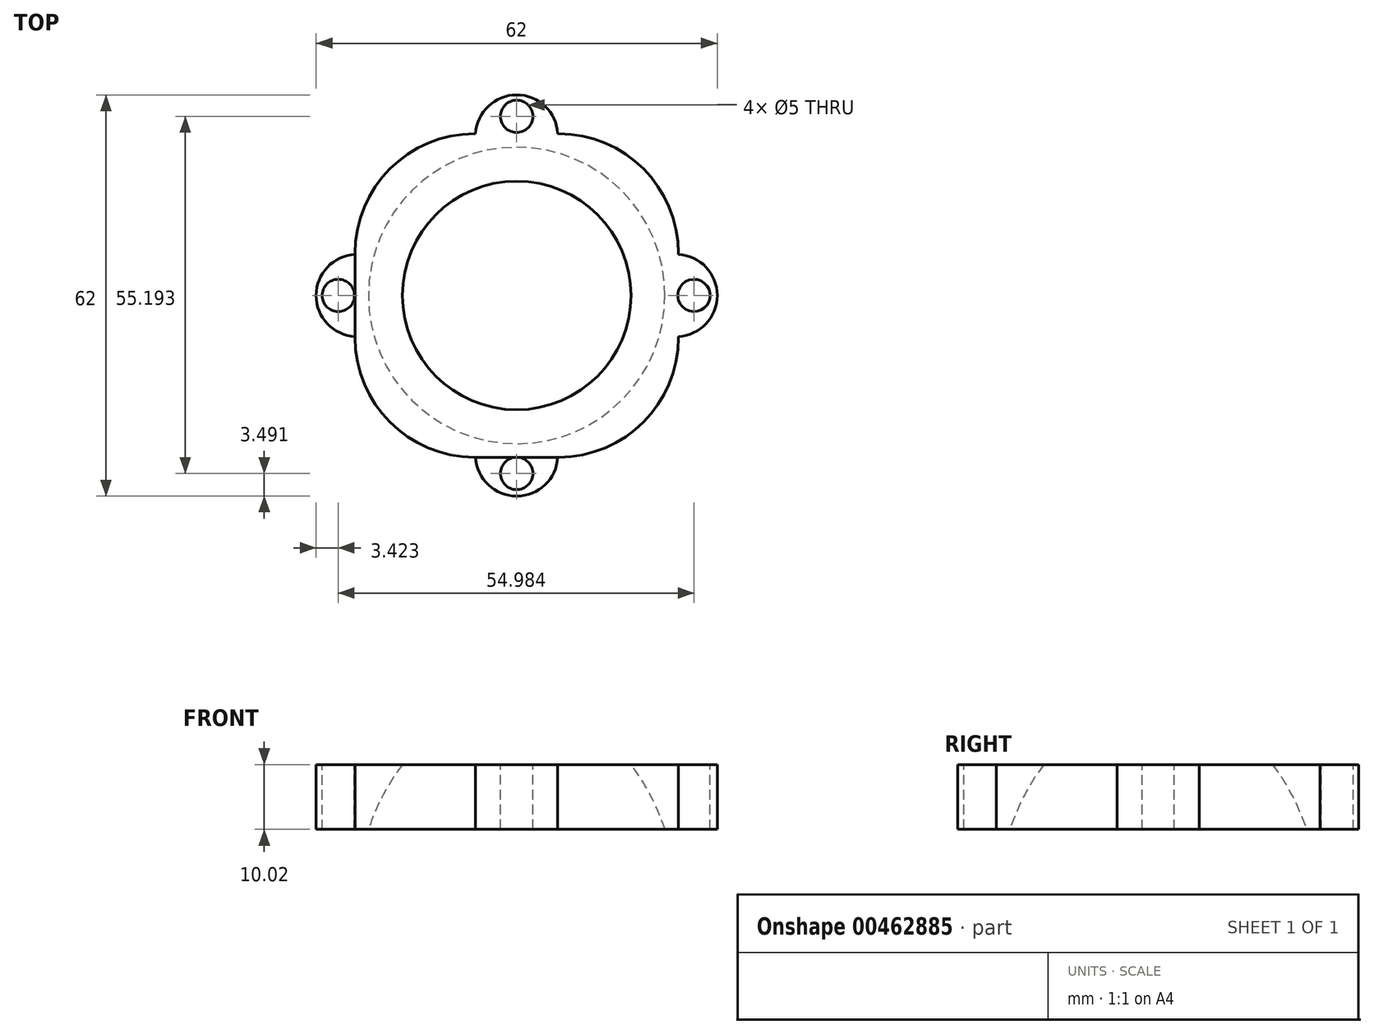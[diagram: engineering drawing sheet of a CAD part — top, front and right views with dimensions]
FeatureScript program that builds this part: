
annotation { "Feature Type Name" : "Feature", "Feature Type Description" : "" }
export const myFeature = defineFeature(function(context is Context, id is Id, definition is map)
    precondition{}
    {
        {
            var Q0;
            Q0=qCreatedBy(makeId("Front.planeOp"),FACE);
            var sketch = newSketch(context, id + "F0", { "sketchPlane" : qUnion([Q0])});
            skEllipticalArc(sketch, "E0", {});
            skLineSegment(sketch, "E1", {"start": v(0, 0) * mm, "end": v(0, 32.5) * mm});
            skLineSegment(sketch, "E2", {"start": v(0, 32.5) * mm, "end": v(0, -32.5) * mm});
            skLineSegment(sketch, "E3", {"start": v(0, 0) * mm, "end": v(25, 0) * mm});
            const initialGuessF0  = {"E0": [0, 0, 0, -1, 0.0325, 0.025, 0, 3.141592653589793]};
            skSetInitialGuess(sketch, initialGuessF0);
            skSolve(sketch);
        }
        {
            var Q0;
            {var subQ0=sQuery(id+"F0.wireOp",EDGE,"E0");Q0=makeQuery(id+"F0.imprint","IMPRINT",FACE,{"disambiguationData":[TD([[makeQuery(id+"F0.imprint","IMPRINT",EDGE,{"derivedFrom":subQ0}),1.0]])]});}
            var Q1;
            Q1=sQuery(id+"F0.wireOp",EDGE,"E2");
            revolve(context, id + "F1", {"entities" : qUnion([Q0]), "axis" : qUnion([Q1]), "revolveType" : RevolveType.FULL});
        }
        {
            var Q0;
            Q0=qCreatedBy(makeId("Top.planeOp"),FACE);
            cPlane(context, id + "F2", {"entities" : qUnion([Q0]), "cplaneType" : CPlaneType.OFFSET, "offset" : 13 * mm, "width" : 152.4 * mm, "height" : 152.4 * mm});
        }
        {
            var Q0;
            Q0=qCreatedBy(id+"F2.planeOp",FACE);
            var sketch = newSketch(context, id + "F3", { "sketchPlane" : qUnion([Q0])});
            skLineSegment(sketch, "E4.bottom", {"start": v(25, -25) * mm, "end": v(-25, -25) * mm});
            skLineSegment(sketch, "E4.top", {"start": v(25, 25) * mm, "end": v(-25, 25) * mm});
            skLineSegment(sketch, "E4.left", {"start": v(25, -25) * mm, "end": v(25, 25) * mm});
            skLineSegment(sketch, "E4.right", {"start": v(-25, -25) * mm, "end": v(-25, 25) * mm});
            skPoint(sketch, "E4.middle", {"position": v(0, 0) * mm});
            skSolve(sketch);
        }
        {
            var Q0;
            Q0=qSketchRegion(id+"F3",true);
            extrude(context, id + "F4", {"entities" : qUnion([Q0]), "depth" : 10 * mm});
        }
        {
            var Q0;
            Q0=makeQuery(id+"F1.opRevolve","SWEPT_BODY",BODY,{"disambiguationData":[OSD([sQuery(id+"F0.wireOp",EDGE,"E0"),sQuery(id+"F0.wireOp",EDGE,"E2")])]});
            var Q1;
            Q1=makeQuery(id+"F4.opExtrude","SWEPT_BODY",BODY,{"disambiguationData":[OSD([sQuery(id+"F3.wireOp",EDGE,"E4.bottom"),sQuery(id+"F3.wireOp",EDGE,"E4.top"),sQuery(id+"F3.wireOp",EDGE,"E4.left"),sQuery(id+"F3.wireOp",EDGE,"E4.right")])]});
            booleanBodies(context, id + "F5", {"operationType" : BooleanOperationType.SUBTRACTION, "tools" : qUnion([Q0]), "targets" : qUnion([Q1])});
        }
        {
            var Q0;
            Q0=qCreatedBy(makeId("Front.planeOp"),FACE);
            var Q1;
            Q1=qBodyType(qCreatedBy(id+"F7",EDGE),BodyType.WIRE);
            cPlane(context, id + "F6", {"entities" : qUnion([Q0, Q1]), "cplaneType" : CPlaneType.OFFSET, "offset" : 25 * mm, "width" : 152.4 * mm, "height" : 152.4 * mm});
        }
        {
            var Q0;
            Q0=qCreatedBy(id+"F6.planeOp",FACE);
            var sketch = newSketch(context, id + "F7", { "sketchPlane" : qUnion([Q0])});
            skLineSegment(sketch, "E5.bottom", {"start": v(6.35, 13.01) * mm, "end": v(-6.35, 13.01) * mm});
            skLineSegment(sketch, "E5.top", {"start": v(6.35, 23.01) * mm, "end": v(-6.35, 23.01) * mm});
            skLineSegment(sketch, "E5.left", {"start": v(6.35, 13.01) * mm, "end": v(6.35, 23.01) * mm});
            skLineSegment(sketch, "E5.right", {"start": v(-6.35, 13.01) * mm, "end": v(-6.35, 23.01) * mm});
            skPoint(sketch, "E5.middle", {"position": v(0, 18.01) * mm});
            skSolve(sketch);
        }
        {
            var Q0;
            Q0=makeQuery(id+"F7.imprint","IMPRINT",FACE,{"disambiguationData":[TD([[makeQuery(id+"F7.imprint","IMPRINT",EDGE,{"derivedFrom":sQuery(id+"F7.wireOp",EDGE,"E5.bottom")}),-1.0]])]});
            extrude(context, id + "F8", {"entities" : qUnion([Q0]), "operationType" : NewBodyOperationType.ADD, "depth" : 6 * mm});
        }
        {
            var Q0;
            Q0=qCreatedBy(makeId("Right.planeOp"),FACE);
            cPlane(context, id + "F9", {"entities" : qUnion([Q0]), "cplaneType" : CPlaneType.OFFSET, "offset" : 25 * mm, "width" : 152.4 * mm, "height" : 152.4 * mm});
        }
        {
            var Q0;
            Q0=qCreatedBy(id+"F9.planeOp",FACE);
            var sketch = newSketch(context, id + "F10", { "sketchPlane" : qUnion([Q0])});
            skLineSegment(sketch, "E6.bottom", {"start": v(6.35, 13) * mm, "end": v(-6.35, 13) * mm});
            skLineSegment(sketch, "E6.top", {"start": v(6.35, 23) * mm, "end": v(-6.35, 23) * mm});
            skLineSegment(sketch, "E6.left", {"start": v(6.35, 13) * mm, "end": v(6.35, 23) * mm});
            skLineSegment(sketch, "E6.right", {"start": v(-6.35, 13) * mm, "end": v(-6.35, 23) * mm});
            skPoint(sketch, "E6.middle", {"position": v(0, 18) * mm});
            skSolve(sketch);
        }
        {
            var Q0;
            Q0=makeQuery(id+"F10.imprint","IMPRINT",FACE,{"disambiguationData":[TD([[makeQuery(id+"F10.imprint","IMPRINT",EDGE,{"derivedFrom":sQuery(id+"F10.wireOp",EDGE,"E6.bottom")}),-1.0]])]});
            extrude(context, id + "F11", {"entities" : qUnion([Q0]), "operationType" : NewBodyOperationType.ADD, "depth" : 6 * mm});
        }
        {
            var Q0;
            Q0=qCreatedBy(makeId("Front.planeOp"),FACE);
            cPlane(context, id + "F12", {"entities" : qUnion([Q0]), "cplaneType" : CPlaneType.OFFSET, "offset" : 25 * mm, "oppositeDirection" : true, "width" : 152.4 * mm, "height" : 152.4 * mm});
        }
        {
            var Q0;
            Q0=qCreatedBy(id+"F12.planeOp",FACE);
            var sketch = newSketch(context, id + "F13", { "sketchPlane" : qUnion([Q0])});
            skLineSegment(sketch, "E7.bottom", {"start": v(6.35, 13) * mm, "end": v(-6.35, 13) * mm});
            skLineSegment(sketch, "E7.top", {"start": v(6.35, 23) * mm, "end": v(-6.35, 23) * mm});
            skLineSegment(sketch, "E7.left", {"start": v(6.35, 13) * mm, "end": v(6.35, 23) * mm});
            skLineSegment(sketch, "E7.right", {"start": v(-6.35, 13) * mm, "end": v(-6.35, 23) * mm});
            skPoint(sketch, "E7.middle", {"position": v(0, 18) * mm});
            skSolve(sketch);
        }
        {
            var Q0;
            Q0=makeQuery(id+"F13.imprint","IMPRINT",FACE,{"disambiguationData":[TD([[makeQuery(id+"F13.imprint","IMPRINT",EDGE,{"derivedFrom":sQuery(id+"F13.wireOp",EDGE,"E7.bottom")}),-1.0]])]});
            extrude(context, id + "F14", {"entities" : qUnion([Q0]), "operationType" : NewBodyOperationType.ADD, "oppositeDirection" : true, "depth" : 6 * mm});
        }
        {
            var Q0;
            Q0=qCreatedBy(makeId("Right.planeOp"),FACE);
            cPlane(context, id + "F15", {"entities" : qUnion([Q0]), "cplaneType" : CPlaneType.OFFSET, "offset" : 25 * mm, "oppositeDirection" : true, "width" : 152.4 * mm, "height" : 152.4 * mm});
        }
        {
            var Q0;
            Q0=qCreatedBy(id+"F15.planeOp",FACE);
            var sketch = newSketch(context, id + "F16", { "sketchPlane" : qUnion([Q0])});
            skLineSegment(sketch, "E8.bottom", {"start": v(-6.35, 12.99) * mm, "end": v(6.35, 12.99) * mm});
            skLineSegment(sketch, "E8.top", {"start": v(-6.35, 22.99) * mm, "end": v(6.35, 22.99) * mm});
            skLineSegment(sketch, "E8.left", {"start": v(-6.35, 12.99) * mm, "end": v(-6.35, 22.99) * mm});
            skLineSegment(sketch, "E8.right", {"start": v(6.35, 12.99) * mm, "end": v(6.35, 22.99) * mm});
            skPoint(sketch, "E8.middle", {"position": v(0, 17.99) * mm});
            skSolve(sketch);
        }
        {
            var Q0;
            Q0=makeQuery(id+"F16.imprint","IMPRINT",FACE,{"disambiguationData":[TD([[makeQuery(id+"F16.imprint","IMPRINT",EDGE,{"derivedFrom":sQuery(id+"F16.wireOp",EDGE,"E8.bottom")}),1.0]])]});
            extrude(context, id + "F17", {"entities" : qUnion([Q0]), "operationType" : NewBodyOperationType.ADD, "oppositeDirection" : true, "depth" : 6 * mm});
        }
        {
            var Q0;
            Q0=makeQuery(id+"F14.opExtrude","SWEPT_FACE",FACE,{"disambiguationData":[OSD([sQuery(id+"F13.wireOp",EDGE,"E7.top")])]});
            var sketch = newSketch(context, id + "F18", { "sketchPlane" : qUnion([Q0])});
            skLineSegment(sketch, "E9", {"start": v(0, 35.08) * mm, "end": v(0, 20.28) * mm});
            skPoint(sketch, "E9.endSnap0", {"position": v(0, 25) * mm});
            skPoint(sketch, "E10", {"position": v(0, 27.68) * mm});
            skSolve(sketch);
        }
        {
            var Q0;
            Q0=sQuery(id+"F18.wireOp",VERTEX,"E10");
            var Q1;
            Q1=makeQuery(id+"F4.opExtrude","SWEPT_BODY",BODY,{"disambiguationData":[OSD([sQuery(id+"F3.wireOp",EDGE,"E4.bottom"),sQuery(id+"F3.wireOp",EDGE,"E4.top"),sQuery(id+"F3.wireOp",EDGE,"E4.left"),sQuery(id+"F3.wireOp",EDGE,"E4.right")])]});
            hole(context, id + "F19", {"style" : HoleStyle.SIMPLE, "endStyle" : HoleEndStyle.THROUGH, "holeDiameter" : 5 * mm, "isTappedThrough" : true, "tappedDepth" : 12.7 * mm, "tapClearance" : 3, "locations" : qUnion([Q0]), "scope" : qUnion([Q1])});
        }
        {
            var Q0;
            Q0=makeQuery(id+"F17.opExtrude","SWEPT_FACE",FACE,{"disambiguationData":[OSD([sQuery(id+"F16.wireOp",EDGE,"E8.top")])]});
            var sketch = newSketch(context, id + "F20", { "sketchPlane" : qUnion([Q0])});
            skLineSegment(sketch, "E11", {"start": v(-37.5, 0) * mm, "end": v(-17.65, 0) * mm});
            skPoint(sketch, "E12", {"position": v(-27.58, 0) * mm});
            skSolve(sketch);
        }
        {
            var Q0;
            Q0=sQuery(id+"F20.wireOp",VERTEX,"E12");
            var Q1;
            Q1=makeQuery(id+"F4.opExtrude","SWEPT_BODY",BODY,{"disambiguationData":[OSD([sQuery(id+"F3.wireOp",EDGE,"E4.bottom"),sQuery(id+"F3.wireOp",EDGE,"E4.top"),sQuery(id+"F3.wireOp",EDGE,"E4.left"),sQuery(id+"F3.wireOp",EDGE,"E4.right")])]});
            hole(context, id + "F21", {"style" : HoleStyle.SIMPLE, "endStyle" : HoleEndStyle.THROUGH, "holeDiameter" : 5 * mm, "isTappedThrough" : true, "tappedDepth" : 12.7 * mm, "tapClearance" : 3, "locations" : qUnion([Q0]), "scope" : qUnion([Q1])});
        }
        {
            var Q0;
            Q0=makeQuery(id+"F11.opExtrude","SWEPT_FACE",FACE,{"disambiguationData":[OSD([sQuery(id+"F10.wireOp",EDGE,"E6.top")])]});
            var sketch = newSketch(context, id + "F22", { "sketchPlane" : qUnion([Q0])});
            skLineSegment(sketch, "E13", {"start": v(34.55, 0) * mm, "end": v(20.26, 0) * mm});
            skPoint(sketch, "E13.endSnap0", {"position": v(25, 0) * mm});
            skPoint(sketch, "E14", {"position": v(27.4, 0) * mm});
            skSolve(sketch);
        }
        {
            var Q0;
            Q0=sQuery(id+"F22.wireOp",VERTEX,"E14");
            var Q1;
            Q1=makeQuery(id+"F4.opExtrude","SWEPT_BODY",BODY,{"disambiguationData":[OSD([sQuery(id+"F3.wireOp",EDGE,"E4.bottom"),sQuery(id+"F3.wireOp",EDGE,"E4.top"),sQuery(id+"F3.wireOp",EDGE,"E4.left"),sQuery(id+"F3.wireOp",EDGE,"E4.right")])]});
            hole(context, id + "F23", {"style" : HoleStyle.SIMPLE, "endStyle" : HoleEndStyle.THROUGH, "holeDiameter" : 5 * mm, "isTappedThrough" : true, "tappedDepth" : 12.7 * mm, "tapClearance" : 3, "locations" : qUnion([Q0]), "scope" : qUnion([Q1])});
        }
        {
            var Q0;
            Q0=makeQuery(id+"F8.opExtrude","SWEPT_FACE",FACE,{"disambiguationData":[OSD([sQuery(id+"F7.wireOp",EDGE,"E5.top")])]});
            var sketch = newSketch(context, id + "F24", { "sketchPlane" : qUnion([Q0])});
            skLineSegment(sketch, "E15", {"start": v(0, -34.8) * mm, "end": v(0, -20.22) * mm});
            skPoint(sketch, "E15.endSnap0", {"position": v(0, -25) * mm});
            skPoint(sketch, "E16", {"position": v(0, -27.5) * mm});
            skSolve(sketch);
        }
        {
            var Q0;
            Q0=sQuery(id+"F24.wireOp",VERTEX,"E16");
            var Q1;
            Q1=makeQuery(id+"F4.opExtrude","SWEPT_BODY",BODY,{"disambiguationData":[OSD([sQuery(id+"F3.wireOp",EDGE,"E4.bottom"),sQuery(id+"F3.wireOp",EDGE,"E4.top"),sQuery(id+"F3.wireOp",EDGE,"E4.left"),sQuery(id+"F3.wireOp",EDGE,"E4.right")])]});
            hole(context, id + "F25", {"style" : HoleStyle.SIMPLE, "endStyle" : HoleEndStyle.THROUGH, "holeDiameter" : 5 * mm, "isTappedThrough" : true, "tappedDepth" : 12.7 * mm, "tapClearance" : 3, "locations" : qUnion([Q0]), "scope" : qUnion([Q1])});
        }
        {
            var Q0;
            Q0=makeQuery(id+"F14.opExtrude","CAP_EDGE",EDGE,{"disambiguationData":[OSD([sQuery(id+"F13.wireOp",EDGE,"E7.left")])],"isStart":false});
            var Q1;
            Q1=makeQuery(id+"F14.opExtrude","CAP_EDGE",EDGE,{"disambiguationData":[OSD([sQuery(id+"F13.wireOp",EDGE,"E7.right")])],"isStart":false});
            var Q2;
            Q2=makeQuery(id+"F17.opExtrude","CAP_EDGE",EDGE,{"disambiguationData":[OSD([sQuery(id+"F16.wireOp",EDGE,"E8.right")])],"isStart":false});
            var Q3;
            Q3=makeQuery(id+"F17.opExtrude","CAP_EDGE",EDGE,{"disambiguationData":[OSD([sQuery(id+"F16.wireOp",EDGE,"E8.left")])],"isStart":false});
            var Q4;
            Q4=makeQuery(id+"F8.opExtrude","CAP_EDGE",EDGE,{"disambiguationData":[OSD([sQuery(id+"F7.wireOp",EDGE,"E5.right")])],"isStart":false});
            var Q5;
            Q5=makeQuery(id+"F8.opExtrude","CAP_EDGE",EDGE,{"disambiguationData":[OSD([sQuery(id+"F7.wireOp",EDGE,"E5.left")])],"isStart":false});
            var Q6;
            Q6=makeQuery(id+"F11.opExtrude","CAP_EDGE",EDGE,{"disambiguationData":[OSD([sQuery(id+"F10.wireOp",EDGE,"E6.right")])],"isStart":false});
            var Q7;
            Q7=makeQuery(id+"F11.opExtrude","CAP_EDGE",EDGE,{"disambiguationData":[OSD([sQuery(id+"F10.wireOp",EDGE,"E6.left")])],"isStart":false});
            fillet(context, id + "F26", {"entities" : qUnion([Q0, Q1, Q2, Q3, Q4, Q5, Q6, Q7]), "radius" : 6.35 * mm, "tangentPropagation" : true, "allowEdgeOverflow" : false});
        }
        {
            var Q0;
            Q0=makeQuery(id+"F4.opExtrude","SWEPT_EDGE",EDGE,{"disambiguationData":[OSD([sQuery(id+"F3.wireOp",EDGE,"E4.bottom"),sQuery(id+"F3.wireOp",EDGE,"E4.right")])]});
            var Q1;
            Q1=makeQuery(id+"F4.opExtrude","SWEPT_EDGE",EDGE,{"disambiguationData":[OSD([sQuery(id+"F3.wireOp",EDGE,"E4.top"),sQuery(id+"F3.wireOp",EDGE,"E4.right")])]});
            var Q2;
            Q2=makeQuery(id+"F4.opExtrude","SWEPT_EDGE",EDGE,{"disambiguationData":[OSD([sQuery(id+"F3.wireOp",EDGE,"E4.top"),sQuery(id+"F3.wireOp",EDGE,"E4.left")])]});
            var Q3;
            Q3=makeQuery(id+"F4.opExtrude","SWEPT_EDGE",EDGE,{"disambiguationData":[OSD([sQuery(id+"F3.wireOp",EDGE,"E4.bottom"),sQuery(id+"F3.wireOp",EDGE,"E4.left")])]});
            fillet(context, id + "F27", {"entities" : qUnion([Q0, Q1, Q2, Q3]), "radius" : 18.5 * mm, "tangentPropagation" : true, "allowEdgeOverflow" : false});
        }
    });
